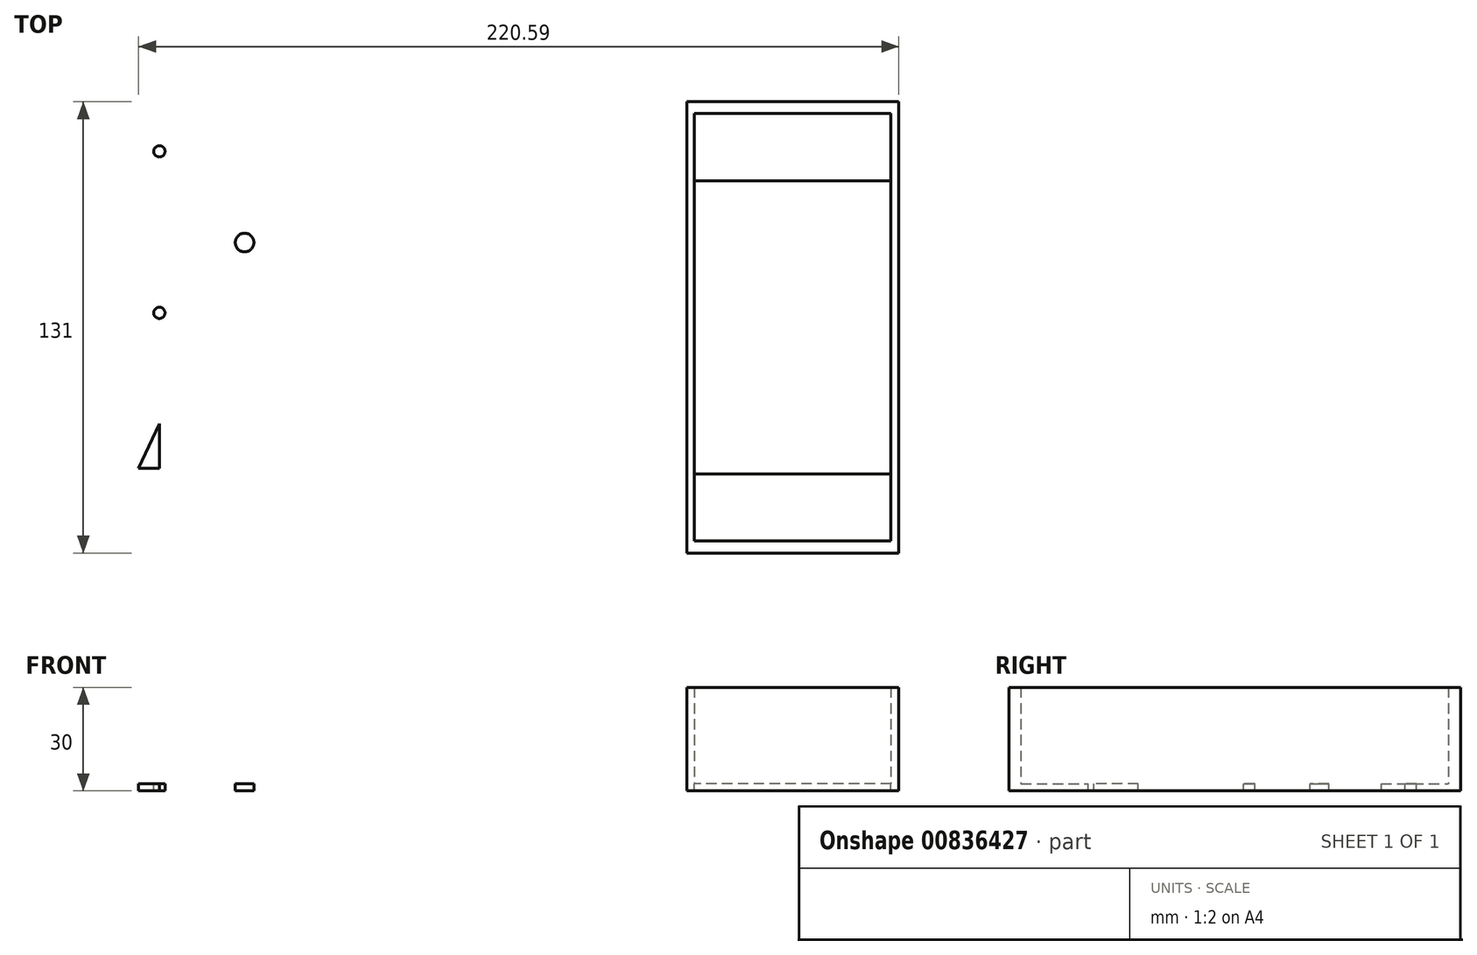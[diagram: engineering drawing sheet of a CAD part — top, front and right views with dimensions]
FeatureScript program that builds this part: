
annotation { "Feature Type Name" : "Feature", "Feature Type Description" : "" }
export const myFeature = defineFeature(function(context is Context, id is Id, definition is map)
    precondition{}
    {
        {
            var Q0;
            Q0=qCreatedBy(makeId("Top.planeOp"),FACE);
            var sketch = newSketch(context, id + "F0", { "sketchPlane" : qUnion([Q0])});
            skLineSegment(sketch, "E0.bottom", {"start": v(28.5, -62.03) * mm, "end": v(-28.5, -62.03) * mm});
            skLineSegment(sketch, "E0.top", {"start": v(28.5, 62.03) * mm, "end": v(-28.5, 62.03) * mm});
            skLineSegment(sketch, "E0.left", {"start": v(28.5, -62.03) * mm, "end": v(28.5, 62.03) * mm});
            skLineSegment(sketch, "E0.right", {"start": v(-28.5, -62.03) * mm, "end": v(-28.5, 62.03) * mm});
            skPoint(sketch, "E0.middle", {"position": v(0, 0) * mm});
            skLineSegment(sketch, "E1.bottom", {"start": v(30.77, -65.5) * mm, "end": v(-30.77, -65.5) * mm});
            skLineSegment(sketch, "E1.top", {"start": v(30.77, 65.5) * mm, "end": v(-30.77, 65.5) * mm});
            skLineSegment(sketch, "E1.left", {"start": v(30.77, -65.5) * mm, "end": v(30.77, 65.5) * mm});
            skLineSegment(sketch, "E1.right", {"start": v(-30.77, -65.5) * mm, "end": v(-30.77, 65.5) * mm});
            skSolve(sketch);
        }
        {
            var Q0;
            Q0=makeQuery(id+"F0.imprint","IMPRINT",FACE,{"disambiguationData":[TD([[makeQuery(id+"F0.imprint","IMPRINT",EDGE,{"derivedFrom":sQuery(id+"F0.wireOp",EDGE,"E0.bottom")}),1.0]])]});
            var Q1;
            Q1=sQuery(id+"F0.wireOp",EDGE,"E1.bottom");
            var Q2;
            Q2=sQuery(id+"F0.wireOp",EDGE,"E0.bottom");
            extrude(context, id + "F1", {"entities" : qUnion([Q0]), "surfaceEntities" : qUnion([Q1, Q2]), "depth" : 30 * mm, "offsetDistance" : 25 * mm});
        }
        {
            var Q0;
            Q0=makeQuery(id+"F0.imprint","IMPRINT",FACE,{"disambiguationData":[TD([[makeQuery(id+"F0.imprint","IMPRINT",EDGE,{"derivedFrom":sQuery(id+"F0.wireOp",EDGE,"E0.bottom")}),-1.0]])]});
            extrude(context, id + "F2", {"entities" : qUnion([Q0]), "operationType" : NewBodyOperationType.ADD, "depth" : 2 * mm, "offsetDistance" : 25 * mm});
        }
        {
            var Q0;
            Q0=makeQuery(id+"F2.opExtrude","CAP_FACE",FACE,{"disambiguationData":[OSD([sQuery(id+"F0.wireOp",EDGE,"E0.bottom"),sQuery(id+"F0.wireOp",EDGE,"E0.top"),sQuery(id+"F0.wireOp",EDGE,"E0.left"),sQuery(id+"F0.wireOp",EDGE,"E0.right")])],"isStart":false});
            var sketch = newSketch(context, id + "F3", { "sketchPlane" : qUnion([Q0])});
            skLineSegment(sketch, "E2.bottom", {"start": v(28.5, 42.52) * mm, "end": v(-28.5, 42.52) * mm});
            skLineSegment(sketch, "E2.top", {"start": v(28.5, -42.52) * mm, "end": v(-28.5, -42.52) * mm});
            skLineSegment(sketch, "E2.left", {"start": v(28.5, 42.52) * mm, "end": v(28.5, -42.52) * mm});
            skLineSegment(sketch, "E2.right", {"start": v(-28.5, 42.52) * mm, "end": v(-28.5, -42.52) * mm});
            skPoint(sketch, "E2.middle", {"position": v(0, 0) * mm});
            skSolve(sketch);
        }
        {
            var Q0;
            Q0=makeQuery(id+"F3.imprint","IMPRINT",FACE,{"disambiguationData":[TD([[makeQuery(id+"F3.imprint","IMPRINT",EDGE,{"derivedFrom":sQuery(id+"F3.wireOp",EDGE,"E2.bottom")}),1.0]])]});
            extrude(context, id + "F4", {"entities" : qUnion([Q0]), "operationType" : NewBodyOperationType.REMOVE, "oppositeDirection" : true, "depth" : 25 * mm, "offsetDistance" : 25 * mm});
        }
        {
            var Q0;
            Q0=qCreatedBy(makeId("Top.planeOp"),FACE);
            var sketch = newSketch(context, id + "F5", { "sketchPlane" : qUnion([Q0])});
            skLineSegment(sketch, "E3.bottom", {"start": v(-130.56, -37.42) * mm, "end": v(-187.55, -37.42) * mm});
            skLineSegment(sketch, "E3.top", {"start": v(-130.56, 86.63) * mm, "end": v(-187.55, 86.63) * mm});
            skLineSegment(sketch, "E3.left", {"start": v(-130.56, -37.42) * mm, "end": v(-130.56, 86.63) * mm});
            skLineSegment(sketch, "E3.right", {"start": v(-187.55, -37.42) * mm, "end": v(-187.55, 86.63) * mm});
            skPoint(sketch, "E3.middle", {"position": v(-159.06, 24.6) * mm});
            skLineSegment(sketch, "E4.bottom", {"start": v(-128.29, -40.9) * mm, "end": v(-189.82, -40.9) * mm});
            skLineSegment(sketch, "E4.top", {"start": v(-128.29, 90.1) * mm, "end": v(-189.82, 90.1) * mm});
            skLineSegment(sketch, "E4.left", {"start": v(-128.29, -40.9) * mm, "end": v(-128.29, 90.1) * mm});
            skLineSegment(sketch, "E4.right", {"start": v(-189.82, -40.9) * mm, "end": v(-189.82, 90.1) * mm});
            skSolve(sketch);
        }
        {
            var Q0;
            Q0 = qSketchRegion(id + "F5", true);
            var Q1;
            Q1=makeQuery(id+"F5.imprint","IMPRINT",FACE,{"disambiguationData":[TD([[makeQuery(id+"F5.imprint","IMPRINT",EDGE,{"derivedFrom":sQuery(id+"F5.wireOp",EDGE,"E3.bottom")}),-1.0]])]});
            extrude(context, id + "F6", {"entities" : qUnion([Q0, Q1]), "depth" : 2 * mm, "offsetDistance" : 25 * mm});
        }
        {
            var Q0;
            Q0=makeQuery(id+"F6.opExtrude","CAP_FACE",FACE,{"disambiguationData":[OSD([sQuery(id+"F5.wireOp",EDGE,"E4.bottom"),sQuery(id+"F5.wireOp",EDGE,"E4.top"),sQuery(id+"F5.wireOp",EDGE,"E4.left"),sQuery(id+"F5.wireOp",EDGE,"E4.right")])],"isStart":false});
            var sketch = newSketch(context, id + "F7", { "sketchPlane" : qUnion([Q0])});
            skPoint(sketch, "E5", {"position": v(-189.82, 90.1) * mm});
            skLineSegment(sketch, "E6", {"start": v(-189.82, 90.1) * mm, "end": v(-183.77, 90.1) * mm});
            skLineSegment(sketch, "E7", {"start": v(-183.77, 90.1) * mm, "end": v(-183.77, -40.9) * mm});
            skLineSegment(sketch, "E8", {"start": v(-189.82, 90.1) * mm, "end": v(-189.82, 51.08) * mm});
            skLineSegment(sketch, "E9", {"start": v(-189.82, -40.9) * mm, "end": v(-189.82, 4.2) * mm});
            skPoint(sketch, "E10", {"position": v(-183.77, 51.08) * mm});
            skPoint(sketch, "E11", {"position": v(-183.77, 4.2) * mm});
            skLineSegment(sketch, "E12", {"start": v(-128.29, 90.1) * mm, "end": v(-189.82, -40.9) * mm});
            skPoint(sketch, "E13", {"position": v(-159.06, 24.6) * mm});
            skCircle(sketch, "E14", {"center": v(-183.77, 51.08) * mm, "radius": 1.64 * mm});
            skCircle(sketch, "E15", {"center": v(-183.77, 4.2) * mm, "radius": 1.64 * mm});
            skCircle(sketch, "E16", {"center": v(-159.06, 24.6) * mm, "radius": 2.7 * mm});
            skSolve(sketch);
        }
        {
            var Q0;
            {var subQ0=sQuery(id+"F7.wireOp",EDGE,"E14");var subQ1=sQuery(id+"F7.wireOp",EDGE,"E7");var subQ2=makeQuery(id+"F7.imprint","INTERSECT",VERTEX,{"disambiguationData":[OD(0.0)],"derivedFrom":[subQ1,subQ0]});Q0=makeQuery(id+"F7.imprint","IMPRINT",FACE,{"disambiguationData":[TD([[makeQuery(id+"F7.imprint","IMPRINT",EDGE,{"disambiguationData":[TD([[subQ2,-1.0]])],"derivedFrom":subQ1}),-1.0]])]});}
            var Q1;
            {var subQ0=sQuery(id+"F7.wireOp",EDGE,"E14");var subQ1=sQuery(id+"F7.wireOp",EDGE,"E7");var subQ2=makeQuery(id+"F7.imprint","INTERSECT",VERTEX,{"disambiguationData":[OD(0.0)],"derivedFrom":[subQ1,subQ0]});Q1=makeQuery(id+"F7.imprint","IMPRINT",FACE,{"disambiguationData":[TD([[makeQuery(id+"F7.imprint","IMPRINT",EDGE,{"disambiguationData":[TD([[subQ2,-1.0]])],"derivedFrom":subQ1}),1.0]])]});}
            var Q2;
            {var subQ0=sQuery(id+"F7.wireOp",EDGE,"E16");var subQ1=sQuery(id+"F7.wireOp",EDGE,"E12");var subQ2=makeQuery(id+"F7.imprint","INTERSECT",VERTEX,{"disambiguationData":[OD(0.0)],"derivedFrom":[subQ1,subQ0]});Q2=makeQuery(id+"F7.imprint","IMPRINT",FACE,{"disambiguationData":[TD([[makeQuery(id+"F7.imprint","IMPRINT",EDGE,{"disambiguationData":[TD([[subQ2,-1.0]])],"derivedFrom":subQ1}),1.0]])]});}
            var Q3;
            {var subQ0=sQuery(id+"F7.wireOp",EDGE,"E16");var subQ1=sQuery(id+"F7.wireOp",EDGE,"E12");var subQ2=makeQuery(id+"F7.imprint","INTERSECT",VERTEX,{"disambiguationData":[OD(0.0)],"derivedFrom":[subQ1,subQ0]});Q3=makeQuery(id+"F7.imprint","IMPRINT",FACE,{"disambiguationData":[TD([[makeQuery(id+"F7.imprint","IMPRINT",EDGE,{"disambiguationData":[TD([[subQ2,-1.0]])],"derivedFrom":subQ1}),-1.0]])]});}
            var Q4;
            {var subQ0=sQuery(id+"F7.wireOp",EDGE,"E15");var subQ1=sQuery(id+"F7.wireOp",EDGE,"E7");var subQ2=makeQuery(id+"F7.imprint","INTERSECT",VERTEX,{"disambiguationData":[OD(0.0)],"derivedFrom":[subQ1,subQ0]});Q4=makeQuery(id+"F7.imprint","IMPRINT",FACE,{"disambiguationData":[TD([[makeQuery(id+"F7.imprint","IMPRINT",EDGE,{"disambiguationData":[TD([[subQ2,-1.0]])],"derivedFrom":subQ1}),1.0]])]});}
            var Q5;
            {var subQ0=sQuery(id+"F7.wireOp",EDGE,"E15");var subQ1=sQuery(id+"F7.wireOp",EDGE,"E7");var subQ2=makeQuery(id+"F7.imprint","INTERSECT",VERTEX,{"disambiguationData":[OD(0.0)],"derivedFrom":[subQ1,subQ0]});Q5=makeQuery(id+"F7.imprint","IMPRINT",FACE,{"disambiguationData":[TD([[makeQuery(id+"F7.imprint","IMPRINT",EDGE,{"disambiguationData":[TD([[subQ2,-1.0]])],"derivedFrom":subQ1}),-1.0]])]});}
            extrude(context, id + "F8", {"entities" : qUnion([Q0, Q1, Q2, Q3, Q4, Q5]), "operationType" : NewBodyOperationType.REMOVE, "oppositeDirection" : true, "depth" : 25 * mm, "offsetDistance" : 25 * mm});
        }
    });
